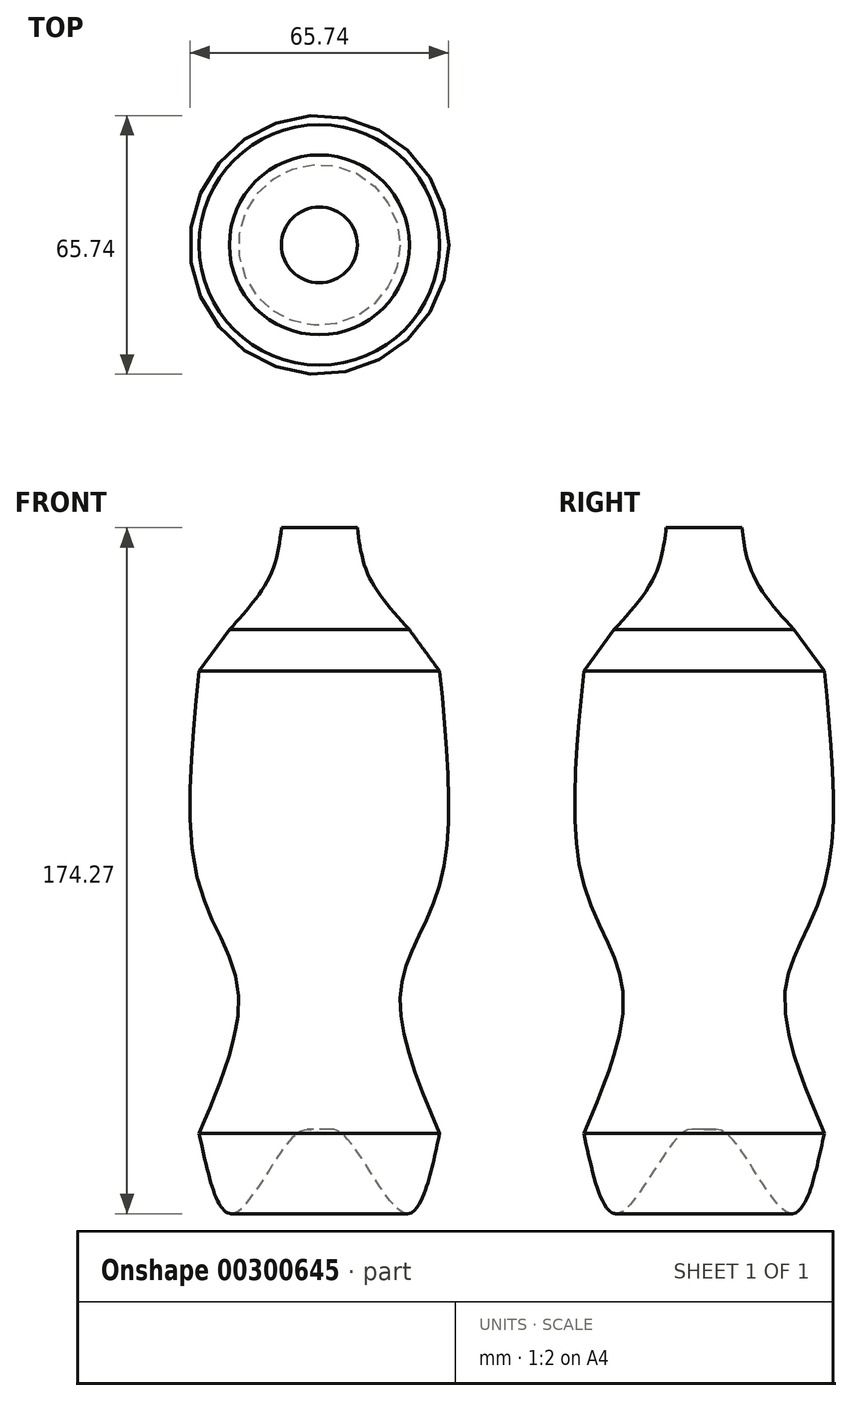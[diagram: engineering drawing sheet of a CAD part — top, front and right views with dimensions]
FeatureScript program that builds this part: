
annotation { "Feature Type Name" : "Feature", "Feature Type Description" : "" }
export const myFeature = defineFeature(function(context is Context, id is Id, definition is map)
    precondition{}
    {
        {
            var Q0;
            Q0=qCreatedBy(makeId("Front.planeOp"),FACE);
            var sketch = newSketch(context, id + "F0", { "sketchPlane" : qUnion([Q0])});
            skFitSpline(sketch, "E0", {"points": [v(-51.43, -80.3) * mm, v(-51.43, -12.99) * mm, v(-45.83, -8.18) * mm, v(-51.43, -4.97) * mm, v(-51.43, 52.4) * mm, v(-29.8, 65.23) * mm, v(-25.63, 70.68) * mm, v(-25.63, 71) * mm, v(-25.63, 70.68) * mm], "startDerivative": vector(-37.36, 313.94) * mm, "endDerivative": vector(0.7, -24.22) * mm});
            skLineSegment(sketch, "E1", {"start": v(-25.63, 71) * mm, "end": v(-25.63, 71) * mm});
            skLineSegment(sketch, "E2", {"start": v(-25.63, 71) * mm, "end": v(-26.63, 71.23) * mm});
            skLineSegment(sketch, "E3", {"start": v(-26.63, 71.23) * mm, "end": v(-25.63, 71.46) * mm});
            skLineSegment(sketch, "E4", {"start": v(-25.63, 71.46) * mm, "end": v(-26.63, 71.66) * mm});
            skLineSegment(sketch, "E5", {"start": v(-26.63, 71.66) * mm, "end": v(-25.63, 71.83) * mm});
            skLineSegment(sketch, "E6", {"start": v(-25.63, 71.83) * mm, "end": v(-26.63, 72) * mm});
            skLineSegment(sketch, "E7", {"start": v(-26.63, 72) * mm, "end": v(-25.63, 72.22) * mm});
            skLineSegment(sketch, "E8", {"start": v(-25.63, 72.22) * mm, "end": v(-26.63, 72.4) * mm});
            skLineSegment(sketch, "E9", {"start": v(-26.63, 72.4) * mm, "end": v(-25.63, 72.59) * mm});
            skLineSegment(sketch, "E10", {"start": v(-25.63, 72.59) * mm, "end": v(-26.63, 72.77) * mm});
            skLineSegment(sketch, "E11", {"start": v(-26.63, 72.77) * mm, "end": v(-25.63, 72.97) * mm});
            skLineSegment(sketch, "E12", {"start": v(-25.63, 72.97) * mm, "end": v(-26.63, 73.15) * mm});
            skLineSegment(sketch, "E13", {"start": v(-26.63, 73.15) * mm, "end": v(-25.63, 73.35) * mm});
            skLineSegment(sketch, "E14", {"start": v(-25.63, 73.35) * mm, "end": v(-26.63, 73.53) * mm});
            skPoint(sketch, "E15.end.orphan", {"position": v(-20.1, 71) * mm});
            skPoint(sketch, "E16.start.orphan", {"position": v(-20.1, -64.67) * mm});
            skLineSegment(sketch, "E17", {"start": v(-20.1, 73.53) * mm, "end": v(-10.48, 73.53) * mm});
            skLineSegment(sketch, "E18", {"start": v(-10.48, 73.53) * mm, "end": v(-10.48, -80.3) * mm});
            skPoint(sketch, "E19.start.orphan", {"position": v(0, 86.9) * mm});
            skLineSegment(sketch, "E20", {"start": v(-10.48, 73.53) * mm, "end": v(-10.48, -111.46) * mm, "construction": true});
            skPoint(sketch, "E21.end.orphan", {"position": v(-48.58, 77.85) * mm});
            skPoint(sketch, "E22.end.orphan", {"position": v(-48.58, 69.8) * mm});
            skFitSpline(sketch, "E23", {"points": [v(-33.33, 47.62) * mm, v(-23.07, 61.2) * mm, v(-20.1, 73.53) * mm], "startDerivative": vector(22.53, 24.97) * mm, "endDerivative": vector(3.44, 26.9) * mm});
            skPoint(sketch, "E24.1.internal.orphan", {"position": v(-41.04, -48.63) * mm});
            skPoint(sketch, "E24.2.internal.orphan", {"position": v(-51.43, -28.93) * mm});
            skFitSpline(sketch, "E25", {"points": [v(-41.04, -80.3) * mm, v(-31.1, -43.91) * mm, v(-41.04, -17.28) * mm, v(-41.04, 37.08) * mm], "startDerivative": vector(50.98, 119.24) * mm, "endDerivative": vector(15.35, 153.86) * mm});
            skLineSegment(sketch, "E26", {"start": v(-33.33, 47.62) * mm, "end": v(-41.04, 37.08) * mm});
            skFitSpline(sketch, "E27", {"points": [v(-41.04, -80.3) * mm, v(-32.2, -100.64) * mm, v(-16.1, -80.3) * mm, v(-10.48, -80.3) * mm], "startDerivative": vector(17.84, -83.64) * mm, "endDerivative": vector(26.49, -13.06) * mm});
            skSolve(sketch);
        }
        {
            var Q0;
            Q0=makeQuery(id+"F0.imprint","IMPRINT",FACE,{"disambiguationData":[TD([[makeQuery(id+"F0.imprint","IMPRINT",EDGE,{"derivedFrom":sQuery(id+"F0.wireOp",EDGE,"E17")}),-1.0]])]});
            var Q1;
            Q1=sQuery(id+"F0.wireOp",EDGE,"E20");
            revolve(context, id + "F1", {"entities" : qUnion([Q0]), "axis" : qUnion([Q1]), "revolveType" : RevolveType.FULL});
        }
    });
